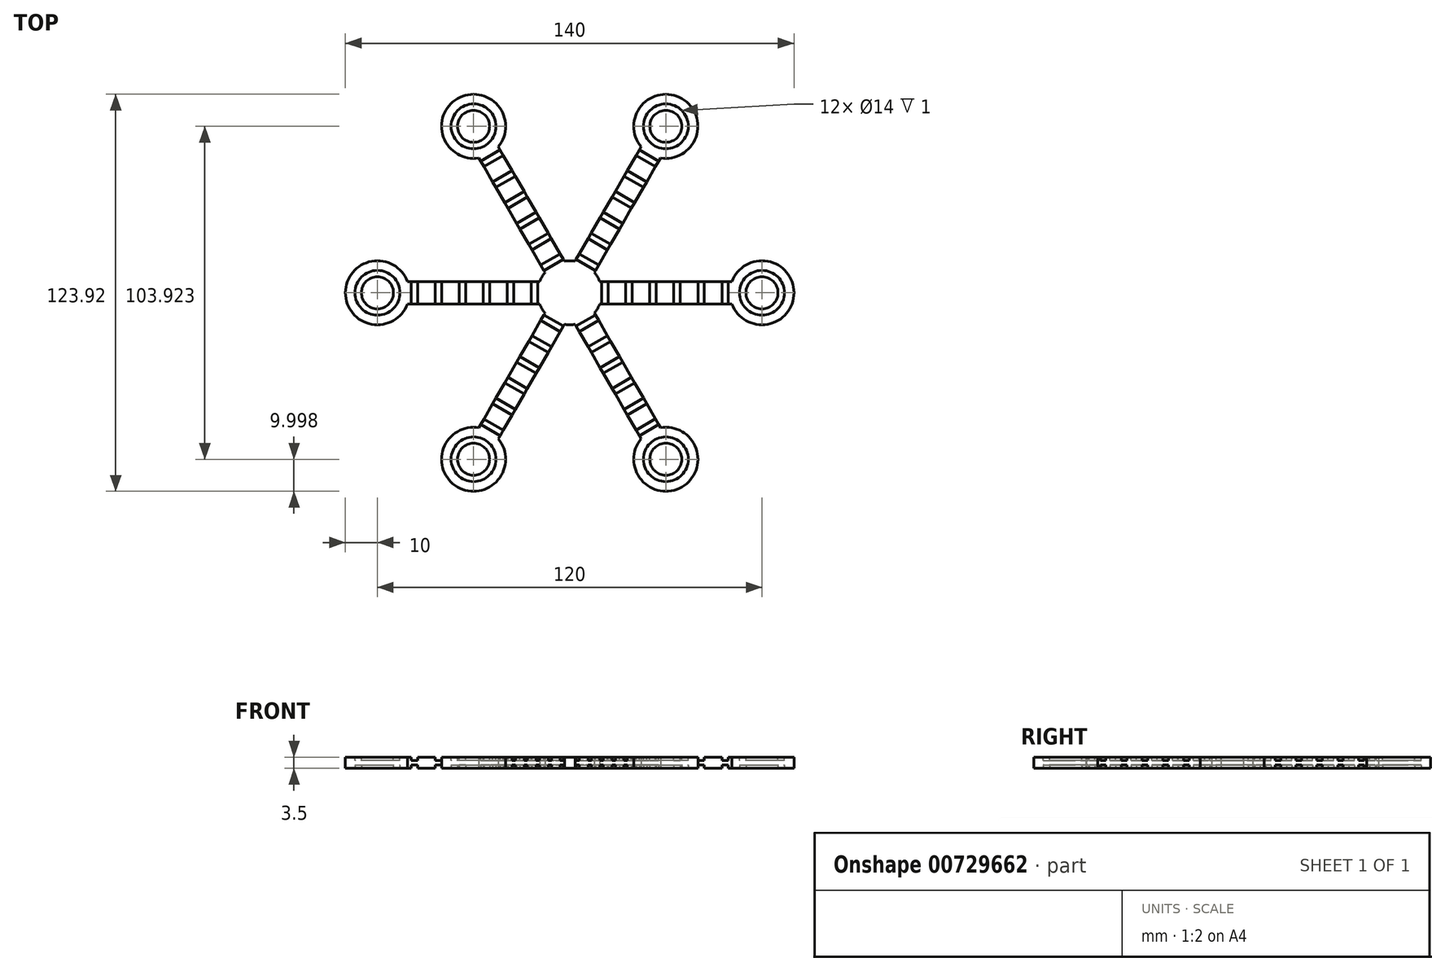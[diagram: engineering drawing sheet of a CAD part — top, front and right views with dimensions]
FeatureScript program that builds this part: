
annotation { "Feature Type Name" : "Feature", "Feature Type Description" : "" }
export const myFeature = defineFeature(function(context is Context, id is Id, definition is map)
    precondition{}
    {
        {
            var Q0;
            Q0=qCreatedBy(makeId("Top.planeOp"),FACE);
            var sketch = newSketch(context, id + "F0", { "sketchPlane" : qUnion([Q0])});
            skCircle(sketch, "E0", {"center": v(0, 0) * mm, "radius": 10 * mm});
            skLineSegment(sketch, "E1.bottom", {"start": v(9.37, 3.5) * mm, "end": v(60.15, 3.5) * mm});
            skLineSegment(sketch, "E1.top", {"start": v(9.37, -3.5) * mm, "end": v(59.85, -3.5) * mm});
            skLineSegment(sketch, "E1.right", {"start": v(60.15, 3.5) * mm, "end": v(59.85, -3.5) * mm});
            skCircle(sketch, "E2", {"center": v(60, 0) * mm, "radius": 10 * mm});
            skLineSegment(sketch, "E3.1.0", {"start": v(1.65, 9.86) * mm, "end": v(27.04, 53.84) * mm});
            skLineSegment(sketch, "E3.1.1", {"start": v(7.71, 6.37) * mm, "end": v(32.95, 50.08) * mm});
            skCircle(sketch, "E3.1.2", {"center": v(30, 51.96) * mm, "radius": 10 * mm});
            skLineSegment(sketch, "E3.1.3", {"start": v(27.04, 53.84) * mm, "end": v(32.95, 50.08) * mm});
            skLineSegment(sketch, "E3.2.0", {"start": v(-7.71, 6.36) * mm, "end": v(-33.1, 50.34) * mm});
            skLineSegment(sketch, "E3.2.1", {"start": v(-1.66, 9.86) * mm, "end": v(-26.9, 53.58) * mm});
            skCircle(sketch, "E3.2.2", {"center": v(-30, 51.96) * mm, "radius": 10 * mm});
            skLineSegment(sketch, "E3.2.3", {"start": v(-33.1, 50.34) * mm, "end": v(-26.9, 53.58) * mm});
            skLineSegment(sketch, "E3.3.0", {"start": v(-9.37, -3.5) * mm, "end": v(-60.15, -3.5) * mm});
            skLineSegment(sketch, "E3.3.1", {"start": v(-9.37, 3.5) * mm, "end": v(-59.85, 3.5) * mm});
            skCircle(sketch, "E3.3.2", {"center": v(-60, 0) * mm, "radius": 10 * mm});
            skLineSegment(sketch, "E3.3.3", {"start": v(-60.15, -3.5) * mm, "end": v(-59.85, 3.5) * mm});
            skLineSegment(sketch, "E3.4.0", {"start": v(-1.65, -9.86) * mm, "end": v(-27.04, -53.84) * mm});
            skLineSegment(sketch, "E3.4.1", {"start": v(-7.71, -6.37) * mm, "end": v(-32.95, -50.08) * mm});
            skCircle(sketch, "E3.4.2", {"center": v(-30, -51.96) * mm, "radius": 10 * mm});
            skLineSegment(sketch, "E3.4.3", {"start": v(-27.04, -53.84) * mm, "end": v(-32.95, -50.08) * mm});
            skLineSegment(sketch, "E3.5.0", {"start": v(7.71, -6.36) * mm, "end": v(33.1, -50.34) * mm});
            skLineSegment(sketch, "E3.5.1", {"start": v(1.66, -9.86) * mm, "end": v(26.9, -53.58) * mm});
            skCircle(sketch, "E3.5.2", {"center": v(30, -51.96) * mm, "radius": 10 * mm});
            skLineSegment(sketch, "E3.5.3", {"start": v(33.1, -50.34) * mm, "end": v(26.9, -53.58) * mm});
            skSolve(sketch);
        }
        {
            var Q0;
            {var subQ0=sQuery(id+"F0.wireOp",EDGE,"E3.3.3");Q0=makeQuery(id+"F0.imprint","IMPRINT",FACE,{"disambiguationData":[TD([[makeQuery(id+"F0.imprint","IMPRINT",EDGE,{"derivedFrom":subQ0}),1.0]])]});}
            var Q1;
            {var subQ0=sQuery(id+"F0.wireOp",EDGE,"E3.3.0");var subQ1=sQuery(id+"F0.wireOp",EDGE,"E0");var subQ2=makeQuery(id+"F0.imprint","INTERSECT",VERTEX,{"derivedFrom":[subQ1,subQ0]});Q1=makeQuery(id+"F0.imprint","IMPRINT",FACE,{"disambiguationData":[TD([[makeQuery(id+"F0.imprint","IMPRINT",EDGE,{"disambiguationData":[TD([[subQ2,1.0]])],"derivedFrom":subQ1}),-1.0]])]});}
            var Q2;
            {var subQ0=sQuery(id+"F0.wireOp",EDGE,"E3.2.3");Q2=makeQuery(id+"F0.imprint","IMPRINT",FACE,{"disambiguationData":[TD([[makeQuery(id+"F0.imprint","IMPRINT",EDGE,{"derivedFrom":subQ0}),1.0]])]});}
            var Q3;
            {var subQ0=sQuery(id+"F0.wireOp",EDGE,"E3.2.3");Q3=makeQuery(id+"F0.imprint","IMPRINT",FACE,{"disambiguationData":[TD([[makeQuery(id+"F0.imprint","IMPRINT",EDGE,{"derivedFrom":subQ0}),-1.0]])]});}
            var Q4;
            {var subQ0=sQuery(id+"F0.wireOp",EDGE,"E3.3.3");Q4=makeQuery(id+"F0.imprint","IMPRINT",FACE,{"disambiguationData":[TD([[makeQuery(id+"F0.imprint","IMPRINT",EDGE,{"derivedFrom":subQ0}),-1.0]])]});}
            var Q5;
            {var subQ0=sQuery(id+"F0.wireOp",EDGE,"E3.1.3");Q5=makeQuery(id+"F0.imprint","IMPRINT",FACE,{"disambiguationData":[TD([[makeQuery(id+"F0.imprint","IMPRINT",EDGE,{"derivedFrom":subQ0}),1.0]])]});}
            var Q6;
            {var subQ0=sQuery(id+"F0.wireOp",EDGE,"E3.1.3");Q6=makeQuery(id+"F0.imprint","IMPRINT",FACE,{"disambiguationData":[TD([[makeQuery(id+"F0.imprint","IMPRINT",EDGE,{"derivedFrom":subQ0}),-1.0]])]});}
            var Q7;
            {var subQ0=sQuery(id+"F0.wireOp",EDGE,"E3.1.0");var subQ1=sQuery(id+"F0.wireOp",EDGE,"E0");var subQ2=makeQuery(id+"F0.imprint","INTERSECT",VERTEX,{"derivedFrom":[subQ1,subQ0]});Q7=makeQuery(id+"F0.imprint","IMPRINT",FACE,{"disambiguationData":[TD([[makeQuery(id+"F0.imprint","IMPRINT",EDGE,{"disambiguationData":[TD([[subQ2,1.0]])],"derivedFrom":subQ1}),-1.0]])]});}
            var Q8;
            {var subQ0=sQuery(id+"F0.wireOp",EDGE,"E0");var subQ8=makeQuery(id+"F0.imprint","INTERSECT",VERTEX,{"derivedFrom":[subQ0,sQuery(id+"F0.wireOp",EDGE,"E1.bottom")]});Q8=makeQuery(id+"F0.imprint","IMPRINT",FACE,{"disambiguationData":[TD([[makeQuery(id+"F0.imprint","IMPRINT",EDGE,{"disambiguationData":[TD([[subQ8,-1.0]])],"derivedFrom":subQ0}),1.0]])]});}
            var Q9;
            {var subQ0=sQuery(id+"F0.wireOp",EDGE,"E1.bottom");var subQ1=sQuery(id+"F0.wireOp",EDGE,"E0");var subQ2=makeQuery(id+"F0.imprint","INTERSECT",VERTEX,{"derivedFrom":[subQ1,subQ0]});Q9=makeQuery(id+"F0.imprint","IMPRINT",FACE,{"disambiguationData":[TD([[makeQuery(id+"F0.imprint","IMPRINT",EDGE,{"disambiguationData":[TD([[subQ2,1.0]])],"derivedFrom":subQ1}),-1.0]])]});}
            var Q10;
            {var subQ0=sQuery(id+"F0.wireOp",EDGE,"E1.right");Q10=makeQuery(id+"F0.imprint","IMPRINT",FACE,{"disambiguationData":[TD([[makeQuery(id+"F0.imprint","IMPRINT",EDGE,{"derivedFrom":subQ0}),-1.0]])]});}
            var Q11;
            {var subQ0=sQuery(id+"F0.wireOp",EDGE,"E1.right");Q11=makeQuery(id+"F0.imprint","IMPRINT",FACE,{"disambiguationData":[TD([[makeQuery(id+"F0.imprint","IMPRINT",EDGE,{"derivedFrom":subQ0}),1.0]])]});}
            var Q12;
            {var subQ0=sQuery(id+"F0.wireOp",EDGE,"E3.5.3");Q12=makeQuery(id+"F0.imprint","IMPRINT",FACE,{"disambiguationData":[TD([[makeQuery(id+"F0.imprint","IMPRINT",EDGE,{"derivedFrom":subQ0}),1.0]])]});}
            var Q13;
            {var subQ0=sQuery(id+"F0.wireOp",EDGE,"E3.5.3");Q13=makeQuery(id+"F0.imprint","IMPRINT",FACE,{"disambiguationData":[TD([[makeQuery(id+"F0.imprint","IMPRINT",EDGE,{"derivedFrom":subQ0}),-1.0]])]});}
            var Q14;
            {var subQ0=sQuery(id+"F0.wireOp",EDGE,"E3.5.0");var subQ1=sQuery(id+"F0.wireOp",EDGE,"E0");var subQ2=makeQuery(id+"F0.imprint","INTERSECT",VERTEX,{"derivedFrom":[subQ1,subQ0]});Q14=makeQuery(id+"F0.imprint","IMPRINT",FACE,{"disambiguationData":[TD([[makeQuery(id+"F0.imprint","IMPRINT",EDGE,{"disambiguationData":[TD([[subQ2,1.0]])],"derivedFrom":subQ1}),-1.0]])]});}
            var Q15;
            {var subQ0=sQuery(id+"F0.wireOp",EDGE,"E3.4.0");var subQ1=sQuery(id+"F0.wireOp",EDGE,"E0");var subQ2=makeQuery(id+"F0.imprint","INTERSECT",VERTEX,{"derivedFrom":[subQ1,subQ0]});Q15=makeQuery(id+"F0.imprint","IMPRINT",FACE,{"disambiguationData":[TD([[makeQuery(id+"F0.imprint","IMPRINT",EDGE,{"disambiguationData":[TD([[subQ2,1.0]])],"derivedFrom":subQ1}),-1.0]])]});}
            var Q16;
            {var subQ0=sQuery(id+"F0.wireOp",EDGE,"E3.4.3");Q16=makeQuery(id+"F0.imprint","IMPRINT",FACE,{"disambiguationData":[TD([[makeQuery(id+"F0.imprint","IMPRINT",EDGE,{"derivedFrom":subQ0}),-1.0]])]});}
            var Q17;
            {var subQ0=sQuery(id+"F0.wireOp",EDGE,"E3.4.3");Q17=makeQuery(id+"F0.imprint","IMPRINT",FACE,{"disambiguationData":[TD([[makeQuery(id+"F0.imprint","IMPRINT",EDGE,{"derivedFrom":subQ0}),1.0]])]});}
            var Q18;
            {var subQ0=sQuery(id+"F0.wireOp",EDGE,"E3.2.0");var subQ1=sQuery(id+"F0.wireOp",EDGE,"E0");var subQ2=makeQuery(id+"F0.imprint","INTERSECT",VERTEX,{"derivedFrom":[subQ1,subQ0]});Q18=makeQuery(id+"F0.imprint","IMPRINT",FACE,{"disambiguationData":[TD([[makeQuery(id+"F0.imprint","IMPRINT",EDGE,{"disambiguationData":[TD([[subQ2,1.0]])],"derivedFrom":subQ1}),-1.0]])]});}
            extrude(context, id + "F1", {"entities" : qUnion([Q0, Q1, Q2, Q3, Q4, Q5, Q6, Q7, Q8, Q9, Q10, Q11, Q12, Q13, Q14, Q15, Q16, Q17, Q18]), "depth" : 3.5 * mm, "offsetDistance" : 25 * mm});
        }
        {
            var Q0;
            Q0=makeQuery(id+"F1.opExtrude","CAP_FACE",FACE,{"disambiguationData":[OSD([sQuery(id+"F0.wireOp",EDGE,"E0"),sQuery(id+"F0.wireOp",EDGE,"E1.bottom"),sQuery(id+"F0.wireOp",EDGE,"E1.top"),sQuery(id+"F0.wireOp",EDGE,"E2"),sQuery(id+"F0.wireOp",EDGE,"E3.1.0"),sQuery(id+"F0.wireOp",EDGE,"E3.1.1"),sQuery(id+"F0.wireOp",EDGE,"E3.1.2"),sQuery(id+"F0.wireOp",EDGE,"E3.2.0"),sQuery(id+"F0.wireOp",EDGE,"E3.2.1"),sQuery(id+"F0.wireOp",EDGE,"E3.2.2"),sQuery(id+"F0.wireOp",EDGE,"E3.3.0"),sQuery(id+"F0.wireOp",EDGE,"E3.3.1"),sQuery(id+"F0.wireOp",EDGE,"E3.3.2"),sQuery(id+"F0.wireOp",EDGE,"E3.4.0"),sQuery(id+"F0.wireOp",EDGE,"E3.4.1"),sQuery(id+"F0.wireOp",EDGE,"E3.4.2"),sQuery(id+"F0.wireOp",EDGE,"E3.5.0"),sQuery(id+"F0.wireOp",EDGE,"E3.5.1"),sQuery(id+"F0.wireOp",EDGE,"E3.5.2")])],"isStart":false});
            var sketch = newSketch(context, id + "F2", { "sketchPlane" : qUnion([Q0])});
            skLineSegment(sketch, "E4.bottom", {"start": v(10, 3.5) * mm, "end": v(12, 3.5) * mm});
            skLineSegment(sketch, "E4.top", {"start": v(10, -3.5) * mm, "end": v(12, -3.5) * mm});
            skLineSegment(sketch, "E4.left", {"start": v(10, 3.5) * mm, "end": v(10, -3.5) * mm});
            skLineSegment(sketch, "E4.right", {"start": v(12, 3.5) * mm, "end": v(12, -3.5) * mm});
            skLineSegment(sketch, "E5.1.0.0", {"start": v(17.5, -3.5) * mm, "end": v(19.5, -3.5) * mm});
            skLineSegment(sketch, "E5.1.0.1", {"start": v(17.5, 3.5) * mm, "end": v(19.5, 3.5) * mm});
            skLineSegment(sketch, "E5.1.0.2", {"start": v(17.5, 3.5) * mm, "end": v(17.5, -3.5) * mm});
            skLineSegment(sketch, "E5.1.0.3", {"start": v(19.5, 3.5) * mm, "end": v(19.5, -3.5) * mm});
            skLineSegment(sketch, "E5.2.0.0", {"start": v(25, -3.5) * mm, "end": v(27, -3.5) * mm});
            skLineSegment(sketch, "E5.2.0.1", {"start": v(25, 3.5) * mm, "end": v(27, 3.5) * mm});
            skLineSegment(sketch, "E5.2.0.2", {"start": v(25, 3.5) * mm, "end": v(25, -3.5) * mm});
            skLineSegment(sketch, "E5.2.0.3", {"start": v(27, 3.5) * mm, "end": v(27, -3.5) * mm});
            skLineSegment(sketch, "E5.3.0.0", {"start": v(32.5, -3.5) * mm, "end": v(34.5, -3.5) * mm});
            skLineSegment(sketch, "E5.3.0.1", {"start": v(32.5, 3.5) * mm, "end": v(34.5, 3.5) * mm});
            skLineSegment(sketch, "E5.3.0.2", {"start": v(32.5, 3.5) * mm, "end": v(32.5, -3.5) * mm});
            skLineSegment(sketch, "E5.3.0.3", {"start": v(34.5, 3.5) * mm, "end": v(34.5, -3.5) * mm});
            skLineSegment(sketch, "E5.4.0.0", {"start": v(40, -3.5) * mm, "end": v(42, -3.5) * mm});
            skLineSegment(sketch, "E5.4.0.1", {"start": v(40, 3.5) * mm, "end": v(42, 3.5) * mm});
            skLineSegment(sketch, "E5.4.0.2", {"start": v(40, 3.5) * mm, "end": v(40, -3.5) * mm});
            skLineSegment(sketch, "E5.4.0.3", {"start": v(42, 3.5) * mm, "end": v(42, -3.5) * mm});
            skLineSegment(sketch, "E5.direction1", {"start": v(10, -3.5) * mm, "end": v(17.5, -3.5) * mm, "construction": true});
            skLineSegment(sketch, "E6.1.0", {"start": v(5.72, 16.9) * mm, "end": v(11.78, 13.4) * mm});
            skLineSegment(sketch, "E6.1.1", {"start": v(1.97, 10.41) * mm, "end": v(2.97, 12.14) * mm});
            skLineSegment(sketch, "E6.1.2", {"start": v(6.72, 18.64) * mm, "end": v(12.78, 15.14) * mm});
            skLineSegment(sketch, "E6.1.3", {"start": v(15.53, 19.9) * mm, "end": v(16.53, 21.64) * mm});
            skLineSegment(sketch, "E6.1.4", {"start": v(1.97, 10.41) * mm, "end": v(8.03, 6.91) * mm});
            skLineSegment(sketch, "E6.1.5", {"start": v(9.47, 23.4) * mm, "end": v(10.47, 25.13) * mm});
            skLineSegment(sketch, "E6.1.6", {"start": v(8.03, 6.91) * mm, "end": v(11.78, 13.4) * mm, "construction": true});
            skLineSegment(sketch, "E6.1.7", {"start": v(2.97, 12.14) * mm, "end": v(9.03, 8.65) * mm});
            skLineSegment(sketch, "E6.1.8", {"start": v(14.22, 31.63) * mm, "end": v(20.28, 28.13) * mm});
            skLineSegment(sketch, "E6.1.9", {"start": v(9.47, 23.4) * mm, "end": v(15.53, 19.9) * mm});
            skLineSegment(sketch, "E6.1.10", {"start": v(17.97, 38.12) * mm, "end": v(24.03, 34.63) * mm});
            skLineSegment(sketch, "E6.1.11", {"start": v(11.78, 13.4) * mm, "end": v(12.78, 15.14) * mm});
            skLineSegment(sketch, "E6.1.12", {"start": v(13.22, 29.9) * mm, "end": v(14.22, 31.63) * mm});
            skLineSegment(sketch, "E6.1.13", {"start": v(10.47, 25.13) * mm, "end": v(16.53, 21.64) * mm});
            skLineSegment(sketch, "E6.1.14", {"start": v(16.97, 36.4) * mm, "end": v(23.03, 32.9) * mm});
            skLineSegment(sketch, "E6.1.15", {"start": v(5.72, 16.9) * mm, "end": v(6.72, 18.64) * mm});
            skLineSegment(sketch, "E6.1.16", {"start": v(13.22, 29.9) * mm, "end": v(19.28, 26.4) * mm});
            skLineSegment(sketch, "E6.1.17", {"start": v(19.28, 26.4) * mm, "end": v(20.28, 28.13) * mm});
            skLineSegment(sketch, "E6.1.18", {"start": v(16.97, 36.4) * mm, "end": v(17.97, 38.12) * mm});
            skLineSegment(sketch, "E6.1.19", {"start": v(23.03, 32.9) * mm, "end": v(24.03, 34.63) * mm});
            skLineSegment(sketch, "E6.1.20", {"start": v(8.03, 6.91) * mm, "end": v(9.03, 8.65) * mm});
            skLineSegment(sketch, "E6.2.0", {"start": v(-11.78, 13.4) * mm, "end": v(-5.72, 16.9) * mm});
            skLineSegment(sketch, "E6.2.1", {"start": v(-8.03, 6.91) * mm, "end": v(-9.03, 8.64) * mm});
            skLineSegment(sketch, "E6.2.2", {"start": v(-12.78, 15.14) * mm, "end": v(-6.72, 18.63) * mm});
            skLineSegment(sketch, "E6.2.3", {"start": v(-9.47, 23.4) * mm, "end": v(-10.47, 25.13) * mm});
            skLineSegment(sketch, "E6.2.4", {"start": v(-8.03, 6.91) * mm, "end": v(-1.97, 10.4) * mm});
            skLineSegment(sketch, "E6.2.5", {"start": v(-15.53, 19.9) * mm, "end": v(-16.53, 21.63) * mm});
            skLineSegment(sketch, "E6.2.6", {"start": v(-1.97, 10.4) * mm, "end": v(-5.72, 16.9) * mm, "construction": true});
            skLineSegment(sketch, "E6.2.7", {"start": v(-9.03, 8.64) * mm, "end": v(-2.97, 12.14) * mm});
            skLineSegment(sketch, "E6.2.8", {"start": v(-20.28, 28.13) * mm, "end": v(-14.22, 31.62) * mm});
            skLineSegment(sketch, "E6.2.9", {"start": v(-15.53, 19.9) * mm, "end": v(-9.47, 23.4) * mm});
            skLineSegment(sketch, "E6.2.10", {"start": v(-24.03, 34.62) * mm, "end": v(-17.97, 38.12) * mm});
            skLineSegment(sketch, "E6.2.11", {"start": v(-5.72, 16.9) * mm, "end": v(-6.72, 18.63) * mm});
            skLineSegment(sketch, "E6.2.12", {"start": v(-19.28, 26.4) * mm, "end": v(-20.28, 28.13) * mm});
            skLineSegment(sketch, "E6.2.13", {"start": v(-16.53, 21.63) * mm, "end": v(-10.47, 25.13) * mm});
            skLineSegment(sketch, "E6.2.14", {"start": v(-23.03, 32.9) * mm, "end": v(-16.97, 36.39) * mm});
            skLineSegment(sketch, "E6.2.15", {"start": v(-11.78, 13.4) * mm, "end": v(-12.78, 15.14) * mm});
            skLineSegment(sketch, "E6.2.16", {"start": v(-19.28, 26.4) * mm, "end": v(-13.22, 29.9) * mm});
            skLineSegment(sketch, "E6.2.17", {"start": v(-13.22, 29.9) * mm, "end": v(-14.22, 31.62) * mm});
            skLineSegment(sketch, "E6.2.18", {"start": v(-23.03, 32.9) * mm, "end": v(-24.03, 34.62) * mm});
            skLineSegment(sketch, "E6.2.19", {"start": v(-16.97, 36.39) * mm, "end": v(-17.97, 38.12) * mm});
            skLineSegment(sketch, "E6.2.20", {"start": v(-1.97, 10.4) * mm, "end": v(-2.97, 12.14) * mm});
            skLineSegment(sketch, "E6.3.0", {"start": v(-17.5, -3.5) * mm, "end": v(-17.5, 3.5) * mm});
            skLineSegment(sketch, "E6.3.1", {"start": v(-10, -3.5) * mm, "end": v(-12, -3.5) * mm});
            skLineSegment(sketch, "E6.3.2", {"start": v(-19.5, -3.5) * mm, "end": v(-19.5, 3.5) * mm});
            skLineSegment(sketch, "E6.3.3", {"start": v(-25, 3.5) * mm, "end": v(-27, 3.5) * mm});
            skLineSegment(sketch, "E6.3.4", {"start": v(-10, -3.5) * mm, "end": v(-10, 3.5) * mm});
            skLineSegment(sketch, "E6.3.5", {"start": v(-25, -3.5) * mm, "end": v(-27, -3.5) * mm});
            skLineSegment(sketch, "E6.3.6", {"start": v(-10, 3.5) * mm, "end": v(-17.5, 3.5) * mm, "construction": true});
            skLineSegment(sketch, "E6.3.7", {"start": v(-12, -3.5) * mm, "end": v(-12, 3.5) * mm});
            skLineSegment(sketch, "E6.3.8", {"start": v(-34.5, -3.5) * mm, "end": v(-34.5, 3.5) * mm});
            skLineSegment(sketch, "E6.3.9", {"start": v(-25, -3.5) * mm, "end": v(-25, 3.5) * mm});
            skLineSegment(sketch, "E6.3.10", {"start": v(-42, -3.5) * mm, "end": v(-42, 3.5) * mm});
            skLineSegment(sketch, "E6.3.11", {"start": v(-17.5, 3.5) * mm, "end": v(-19.5, 3.5) * mm});
            skLineSegment(sketch, "E6.3.12", {"start": v(-32.5, -3.5) * mm, "end": v(-34.5, -3.5) * mm});
            skLineSegment(sketch, "E6.3.13", {"start": v(-27, -3.5) * mm, "end": v(-27, 3.5) * mm});
            skLineSegment(sketch, "E6.3.14", {"start": v(-40, -3.5) * mm, "end": v(-40, 3.5) * mm});
            skLineSegment(sketch, "E6.3.15", {"start": v(-17.5, -3.5) * mm, "end": v(-19.5, -3.5) * mm});
            skLineSegment(sketch, "E6.3.16", {"start": v(-32.5, -3.5) * mm, "end": v(-32.5, 3.5) * mm});
            skLineSegment(sketch, "E6.3.17", {"start": v(-32.5, 3.5) * mm, "end": v(-34.5, 3.5) * mm});
            skLineSegment(sketch, "E6.3.18", {"start": v(-40, -3.5) * mm, "end": v(-42, -3.5) * mm});
            skLineSegment(sketch, "E6.3.19", {"start": v(-40, 3.5) * mm, "end": v(-42, 3.5) * mm});
            skLineSegment(sketch, "E6.3.20", {"start": v(-10, 3.5) * mm, "end": v(-12, 3.5) * mm});
            skLineSegment(sketch, "E6.4.0", {"start": v(-5.72, -16.9) * mm, "end": v(-11.78, -13.4) * mm});
            skLineSegment(sketch, "E6.4.1", {"start": v(-1.97, -10.41) * mm, "end": v(-2.97, -12.14) * mm});
            skLineSegment(sketch, "E6.4.2", {"start": v(-6.72, -18.64) * mm, "end": v(-12.78, -15.14) * mm});
            skLineSegment(sketch, "E6.4.3", {"start": v(-15.53, -19.9) * mm, "end": v(-16.53, -21.64) * mm});
            skLineSegment(sketch, "E6.4.4", {"start": v(-1.97, -10.41) * mm, "end": v(-8.03, -6.91) * mm});
            skLineSegment(sketch, "E6.4.5", {"start": v(-9.47, -23.4) * mm, "end": v(-10.47, -25.13) * mm});
            skLineSegment(sketch, "E6.4.6", {"start": v(-8.03, -6.91) * mm, "end": v(-11.78, -13.4) * mm, "construction": true});
            skLineSegment(sketch, "E6.4.7", {"start": v(-2.97, -12.14) * mm, "end": v(-9.03, -8.65) * mm});
            skLineSegment(sketch, "E6.4.8", {"start": v(-14.22, -31.63) * mm, "end": v(-20.28, -28.13) * mm});
            skLineSegment(sketch, "E6.4.9", {"start": v(-9.47, -23.4) * mm, "end": v(-15.53, -19.9) * mm});
            skLineSegment(sketch, "E6.4.10", {"start": v(-17.97, -38.12) * mm, "end": v(-24.03, -34.63) * mm});
            skLineSegment(sketch, "E6.4.11", {"start": v(-11.78, -13.4) * mm, "end": v(-12.78, -15.14) * mm});
            skLineSegment(sketch, "E6.4.12", {"start": v(-13.22, -29.9) * mm, "end": v(-14.22, -31.63) * mm});
            skLineSegment(sketch, "E6.4.13", {"start": v(-10.47, -25.13) * mm, "end": v(-16.53, -21.64) * mm});
            skLineSegment(sketch, "E6.4.14", {"start": v(-16.97, -36.4) * mm, "end": v(-23.03, -32.9) * mm});
            skLineSegment(sketch, "E6.4.15", {"start": v(-5.72, -16.9) * mm, "end": v(-6.72, -18.64) * mm});
            skLineSegment(sketch, "E6.4.16", {"start": v(-13.22, -29.9) * mm, "end": v(-19.28, -26.4) * mm});
            skLineSegment(sketch, "E6.4.17", {"start": v(-19.28, -26.4) * mm, "end": v(-20.28, -28.13) * mm});
            skLineSegment(sketch, "E6.4.18", {"start": v(-16.97, -36.4) * mm, "end": v(-17.97, -38.12) * mm});
            skLineSegment(sketch, "E6.4.19", {"start": v(-23.03, -32.9) * mm, "end": v(-24.03, -34.63) * mm});
            skLineSegment(sketch, "E6.4.20", {"start": v(-8.03, -6.91) * mm, "end": v(-9.03, -8.65) * mm});
            skLineSegment(sketch, "E6.5.0", {"start": v(11.78, -13.4) * mm, "end": v(5.72, -16.9) * mm});
            skLineSegment(sketch, "E6.5.1", {"start": v(8.03, -6.91) * mm, "end": v(9.03, -8.64) * mm});
            skLineSegment(sketch, "E6.5.2", {"start": v(12.78, -15.14) * mm, "end": v(6.72, -18.63) * mm});
            skLineSegment(sketch, "E6.5.3", {"start": v(9.47, -23.4) * mm, "end": v(10.47, -25.13) * mm});
            skLineSegment(sketch, "E6.5.4", {"start": v(8.03, -6.91) * mm, "end": v(1.97, -10.4) * mm});
            skLineSegment(sketch, "E6.5.5", {"start": v(15.53, -19.9) * mm, "end": v(16.53, -21.63) * mm});
            skLineSegment(sketch, "E6.5.6", {"start": v(1.97, -10.4) * mm, "end": v(5.72, -16.9) * mm, "construction": true});
            skLineSegment(sketch, "E6.5.7", {"start": v(9.03, -8.64) * mm, "end": v(2.97, -12.14) * mm});
            skLineSegment(sketch, "E6.5.8", {"start": v(20.28, -28.13) * mm, "end": v(14.22, -31.62) * mm});
            skLineSegment(sketch, "E6.5.9", {"start": v(15.53, -19.9) * mm, "end": v(9.47, -23.4) * mm});
            skLineSegment(sketch, "E6.5.10", {"start": v(24.03, -34.62) * mm, "end": v(17.97, -38.12) * mm});
            skLineSegment(sketch, "E6.5.11", {"start": v(5.72, -16.9) * mm, "end": v(6.72, -18.63) * mm});
            skLineSegment(sketch, "E6.5.12", {"start": v(19.28, -26.4) * mm, "end": v(20.28, -28.13) * mm});
            skLineSegment(sketch, "E6.5.13", {"start": v(16.53, -21.63) * mm, "end": v(10.47, -25.13) * mm});
            skLineSegment(sketch, "E6.5.14", {"start": v(23.03, -32.9) * mm, "end": v(16.97, -36.39) * mm});
            skLineSegment(sketch, "E6.5.15", {"start": v(11.78, -13.4) * mm, "end": v(12.78, -15.14) * mm});
            skLineSegment(sketch, "E6.5.16", {"start": v(19.28, -26.4) * mm, "end": v(13.22, -29.9) * mm});
            skLineSegment(sketch, "E6.5.17", {"start": v(13.22, -29.9) * mm, "end": v(14.22, -31.62) * mm});
            skLineSegment(sketch, "E6.5.18", {"start": v(23.03, -32.9) * mm, "end": v(24.03, -34.62) * mm});
            skLineSegment(sketch, "E6.5.19", {"start": v(16.97, -36.39) * mm, "end": v(17.97, -38.12) * mm});
            skLineSegment(sketch, "E6.5.20", {"start": v(1.97, -10.4) * mm, "end": v(2.97, -12.14) * mm});
            skPoint(sketch, "E6.center", {"position": v(0, 0) * mm});
            skCircle(sketch, "E7", {"center": v(60, 0) * mm, "radius": 7 * mm});
            skCircle(sketch, "E8", {"center": v(60, 0) * mm, "radius": 5 * mm});
            skCircle(sketch, "E9.1.0", {"center": v(30, 51.96) * mm, "radius": 7 * mm});
            skCircle(sketch, "E9.1.1", {"center": v(30, 51.96) * mm, "radius": 5 * mm});
            skCircle(sketch, "E9.2.0", {"center": v(-30, 51.96) * mm, "radius": 7 * mm});
            skCircle(sketch, "E9.2.1", {"center": v(-30, 51.96) * mm, "radius": 5 * mm});
            skCircle(sketch, "E9.3.0", {"center": v(-60, 0) * mm, "radius": 7 * mm});
            skCircle(sketch, "E9.3.1", {"center": v(-60, 0) * mm, "radius": 5 * mm});
            skCircle(sketch, "E9.4.0", {"center": v(-30, -51.96) * mm, "radius": 7 * mm});
            skCircle(sketch, "E9.4.1", {"center": v(-30, -51.96) * mm, "radius": 5 * mm});
            skCircle(sketch, "E9.5.0", {"center": v(30, -51.96) * mm, "radius": 7 * mm});
            skCircle(sketch, "E9.5.1", {"center": v(30, -51.96) * mm, "radius": 5 * mm});
            skLineSegment(sketch, "E10.0.5.0", {"start": v(47.5, -3.5) * mm, "end": v(49.5, -3.5) * mm});
            skLineSegment(sketch, "E10.3.5.0", {"start": v(47.5, 3.5) * mm, "end": v(49.5, 3.5) * mm});
            skLineSegment(sketch, "E10.6.5.0", {"start": v(47.5, 3.5) * mm, "end": v(47.5, -3.5) * mm});
            skLineSegment(sketch, "E10.9.5.0", {"start": v(49.5, 3.5) * mm, "end": v(49.5, -3.5) * mm});
            skLineSegment(sketch, "E11.1.0", {"start": v(26.78, 39.39) * mm, "end": v(27.78, 41.12) * mm});
            skLineSegment(sketch, "E11.1.1", {"start": v(20.72, 42.89) * mm, "end": v(26.78, 39.39) * mm});
            skLineSegment(sketch, "E11.1.2", {"start": v(21.72, 44.62) * mm, "end": v(27.78, 41.12) * mm});
            skLineSegment(sketch, "E11.1.3", {"start": v(20.72, 42.89) * mm, "end": v(21.72, 44.62) * mm});
            skLineSegment(sketch, "E11.2.0", {"start": v(-20.72, 42.88) * mm, "end": v(-21.72, 44.61) * mm});
            skLineSegment(sketch, "E11.2.1", {"start": v(-26.78, 39.39) * mm, "end": v(-20.72, 42.88) * mm});
            skLineSegment(sketch, "E11.2.2", {"start": v(-27.78, 41.12) * mm, "end": v(-21.72, 44.61) * mm});
            skLineSegment(sketch, "E11.2.3", {"start": v(-26.78, 39.39) * mm, "end": v(-27.78, 41.12) * mm});
            skLineSegment(sketch, "E11.3.0", {"start": v(-47.5, 3.5) * mm, "end": v(-49.5, 3.5) * mm});
            skLineSegment(sketch, "E11.3.1", {"start": v(-47.5, -3.5) * mm, "end": v(-47.5, 3.5) * mm});
            skLineSegment(sketch, "E11.3.2", {"start": v(-49.5, -3.5) * mm, "end": v(-49.5, 3.5) * mm});
            skLineSegment(sketch, "E11.3.3", {"start": v(-47.5, -3.5) * mm, "end": v(-49.5, -3.5) * mm});
            skLineSegment(sketch, "E11.4.0", {"start": v(-26.78, -39.39) * mm, "end": v(-27.78, -41.12) * mm});
            skLineSegment(sketch, "E11.4.1", {"start": v(-20.72, -42.89) * mm, "end": v(-26.78, -39.39) * mm});
            skLineSegment(sketch, "E11.4.2", {"start": v(-21.72, -44.62) * mm, "end": v(-27.78, -41.12) * mm});
            skLineSegment(sketch, "E11.4.3", {"start": v(-20.72, -42.89) * mm, "end": v(-21.72, -44.62) * mm});
            skLineSegment(sketch, "E11.5.0", {"start": v(20.72, -42.88) * mm, "end": v(21.72, -44.61) * mm});
            skLineSegment(sketch, "E11.5.1", {"start": v(26.78, -39.39) * mm, "end": v(20.72, -42.88) * mm});
            skLineSegment(sketch, "E11.5.2", {"start": v(27.78, -41.12) * mm, "end": v(21.72, -44.61) * mm});
            skLineSegment(sketch, "E11.5.3", {"start": v(26.78, -39.39) * mm, "end": v(27.78, -41.12) * mm});
            skSolve(sketch);
        }
        {
            var Q0;
            Q0=makeQuery(id+"F2.imprint","IMPRINT",FACE,{"disambiguationData":[TD([[makeQuery(id+"F2.imprint","IMPRINT",EDGE,{"derivedFrom":sQuery(id+"F2.wireOp",EDGE,"E6.4.10")}),-1.0]])]});
            var Q1;
            Q1=makeQuery(id+"F2.imprint","IMPRINT",FACE,{"disambiguationData":[TD([[makeQuery(id+"F2.imprint","IMPRINT",EDGE,{"derivedFrom":sQuery(id+"F2.wireOp",EDGE,"E6.4.8")}),-1.0]])]});
            var Q2;
            Q2=makeQuery(id+"F2.imprint","IMPRINT",FACE,{"disambiguationData":[TD([[makeQuery(id+"F2.imprint","IMPRINT",EDGE,{"derivedFrom":sQuery(id+"F2.wireOp",EDGE,"E6.4.3")}),1.0]])]});
            var Q3;
            Q3=makeQuery(id+"F2.imprint","IMPRINT",FACE,{"disambiguationData":[TD([[makeQuery(id+"F2.imprint","IMPRINT",EDGE,{"derivedFrom":sQuery(id+"F2.wireOp",EDGE,"E6.4.0")}),1.0]])]});
            var Q4;
            Q4=makeQuery(id+"F2.imprint","IMPRINT",FACE,{"disambiguationData":[TD([[makeQuery(id+"F2.imprint","IMPRINT",EDGE,{"derivedFrom":sQuery(id+"F2.wireOp",EDGE,"E6.4.1")}),-1.0]])]});
            var Q5;
            Q5=makeQuery(id+"F2.imprint","IMPRINT",FACE,{"disambiguationData":[TD([[makeQuery(id+"F2.imprint","IMPRINT",EDGE,{"derivedFrom":sQuery(id+"F2.wireOp",EDGE,"E6.5.1")}),-1.0]])]});
            var Q6;
            Q6=makeQuery(id+"F2.imprint","IMPRINT",FACE,{"disambiguationData":[TD([[makeQuery(id+"F2.imprint","IMPRINT",EDGE,{"derivedFrom":sQuery(id+"F2.wireOp",EDGE,"E6.5.0")}),1.0]])]});
            var Q7;
            Q7=makeQuery(id+"F2.imprint","IMPRINT",FACE,{"disambiguationData":[TD([[makeQuery(id+"F2.imprint","IMPRINT",EDGE,{"derivedFrom":sQuery(id+"F2.wireOp",EDGE,"E6.5.3")}),1.0]])]});
            var Q8;
            Q8=makeQuery(id+"F2.imprint","IMPRINT",FACE,{"disambiguationData":[TD([[makeQuery(id+"F2.imprint","IMPRINT",EDGE,{"derivedFrom":sQuery(id+"F2.wireOp",EDGE,"E6.5.8")}),-1.0]])]});
            var Q9;
            Q9=makeQuery(id+"F2.imprint","IMPRINT",FACE,{"disambiguationData":[TD([[makeQuery(id+"F2.imprint","IMPRINT",EDGE,{"derivedFrom":sQuery(id+"F2.wireOp",EDGE,"E6.5.10")}),-1.0]])]});
            var Q10;
            Q10=makeQuery(id+"F2.imprint","IMPRINT",FACE,{"disambiguationData":[TD([[makeQuery(id+"F2.imprint","IMPRINT",EDGE,{"derivedFrom":sQuery(id+"F2.wireOp",EDGE,"E5.4.0.0")}),1.0]])]});
            var Q11;
            Q11=makeQuery(id+"F2.imprint","IMPRINT",FACE,{"disambiguationData":[TD([[makeQuery(id+"F2.imprint","IMPRINT",EDGE,{"derivedFrom":sQuery(id+"F2.wireOp",EDGE,"E5.2.0.0")}),1.0]])]});
            var Q12;
            Q12=makeQuery(id+"F2.imprint","IMPRINT",FACE,{"disambiguationData":[TD([[makeQuery(id+"F2.imprint","IMPRINT",EDGE,{"derivedFrom":sQuery(id+"F2.wireOp",EDGE,"E5.1.0.0")}),1.0]])]});
            var Q13;
            Q13=makeQuery(id+"F2.imprint","IMPRINT",FACE,{"disambiguationData":[TD([[makeQuery(id+"F2.imprint","IMPRINT",EDGE,{"derivedFrom":sQuery(id+"F2.wireOp",EDGE,"E4.bottom")}),-1.0]])]});
            var Q14;
            Q14=makeQuery(id+"F2.imprint","IMPRINT",FACE,{"disambiguationData":[TD([[makeQuery(id+"F2.imprint","IMPRINT",EDGE,{"derivedFrom":sQuery(id+"F2.wireOp",EDGE,"E6.1.10")}),-1.0]])]});
            var Q15;
            Q15=makeQuery(id+"F2.imprint","IMPRINT",FACE,{"disambiguationData":[TD([[makeQuery(id+"F2.imprint","IMPRINT",EDGE,{"derivedFrom":sQuery(id+"F2.wireOp",EDGE,"E6.1.8")}),-1.0]])]});
            var Q16;
            Q16=makeQuery(id+"F2.imprint","IMPRINT",FACE,{"disambiguationData":[TD([[makeQuery(id+"F2.imprint","IMPRINT",EDGE,{"derivedFrom":sQuery(id+"F2.wireOp",EDGE,"E6.1.3")}),1.0]])]});
            var Q17;
            Q17=makeQuery(id+"F2.imprint","IMPRINT",FACE,{"disambiguationData":[TD([[makeQuery(id+"F2.imprint","IMPRINT",EDGE,{"derivedFrom":sQuery(id+"F2.wireOp",EDGE,"E6.1.0")}),1.0]])]});
            var Q18;
            Q18=makeQuery(id+"F2.imprint","IMPRINT",FACE,{"disambiguationData":[TD([[makeQuery(id+"F2.imprint","IMPRINT",EDGE,{"derivedFrom":sQuery(id+"F2.wireOp",EDGE,"E6.1.1")}),-1.0]])]});
            var Q19;
            Q19=makeQuery(id+"F2.imprint","IMPRINT",FACE,{"disambiguationData":[TD([[makeQuery(id+"F2.imprint","IMPRINT",EDGE,{"derivedFrom":sQuery(id+"F2.wireOp",EDGE,"E6.2.1")}),-1.0]])]});
            var Q20;
            Q20=makeQuery(id+"F2.imprint","IMPRINT",FACE,{"disambiguationData":[TD([[makeQuery(id+"F2.imprint","IMPRINT",EDGE,{"derivedFrom":sQuery(id+"F2.wireOp",EDGE,"E6.2.0")}),1.0]])]});
            var Q21;
            Q21=makeQuery(id+"F2.imprint","IMPRINT",FACE,{"disambiguationData":[TD([[makeQuery(id+"F2.imprint","IMPRINT",EDGE,{"derivedFrom":sQuery(id+"F2.wireOp",EDGE,"E6.2.3")}),1.0]])]});
            var Q22;
            Q22=makeQuery(id+"F2.imprint","IMPRINT",FACE,{"disambiguationData":[TD([[makeQuery(id+"F2.imprint","IMPRINT",EDGE,{"derivedFrom":sQuery(id+"F2.wireOp",EDGE,"E6.2.8")}),-1.0]])]});
            var Q23;
            Q23=makeQuery(id+"F2.imprint","IMPRINT",FACE,{"disambiguationData":[TD([[makeQuery(id+"F2.imprint","IMPRINT",EDGE,{"derivedFrom":sQuery(id+"F2.wireOp",EDGE,"E6.2.10")}),-1.0]])]});
            var Q24;
            Q24=makeQuery(id+"F2.imprint","IMPRINT",FACE,{"disambiguationData":[TD([[makeQuery(id+"F2.imprint","IMPRINT",EDGE,{"derivedFrom":sQuery(id+"F2.wireOp",EDGE,"E6.3.1")}),-1.0]])]});
            var Q25;
            Q25=makeQuery(id+"F2.imprint","IMPRINT",FACE,{"disambiguationData":[TD([[makeQuery(id+"F2.imprint","IMPRINT",EDGE,{"derivedFrom":sQuery(id+"F2.wireOp",EDGE,"E6.3.0")}),1.0]])]});
            var Q26;
            Q26=makeQuery(id+"F2.imprint","IMPRINT",FACE,{"disambiguationData":[TD([[makeQuery(id+"F2.imprint","IMPRINT",EDGE,{"derivedFrom":sQuery(id+"F2.wireOp",EDGE,"E6.3.3")}),1.0]])]});
            var Q27;
            Q27=makeQuery(id+"F2.imprint","IMPRINT",FACE,{"disambiguationData":[TD([[makeQuery(id+"F2.imprint","IMPRINT",EDGE,{"derivedFrom":sQuery(id+"F2.wireOp",EDGE,"E6.3.8")}),-1.0]])]});
            var Q28;
            Q28=makeQuery(id+"F2.imprint","IMPRINT",FACE,{"disambiguationData":[TD([[makeQuery(id+"F2.imprint","IMPRINT",EDGE,{"derivedFrom":sQuery(id+"F2.wireOp",EDGE,"E6.3.10")}),-1.0]])]});
            var Q29;
            Q29=makeQuery(id+"F2.imprint","IMPRINT",FACE,{"disambiguationData":[TD([[makeQuery(id+"F2.imprint","IMPRINT",EDGE,{"derivedFrom":sQuery(id+"F2.wireOp",EDGE,"E9.2.0")}),1.0]])]});
            var Q30;
            Q30=makeQuery(id+"F2.imprint","IMPRINT",FACE,{"disambiguationData":[TD([[makeQuery(id+"F2.imprint","IMPRINT",EDGE,{"derivedFrom":sQuery(id+"F2.wireOp",EDGE,"E9.1.0")}),1.0]])]});
            var Q31;
            Q31=makeQuery(id+"F2.imprint","IMPRINT",FACE,{"disambiguationData":[TD([[makeQuery(id+"F2.imprint","IMPRINT",EDGE,{"derivedFrom":sQuery(id+"F2.wireOp",EDGE,"E7")}),1.0]])]});
            var Q32;
            Q32=makeQuery(id+"F2.imprint","IMPRINT",FACE,{"disambiguationData":[TD([[makeQuery(id+"F2.imprint","IMPRINT",EDGE,{"derivedFrom":sQuery(id+"F2.wireOp",EDGE,"E9.5.0")}),1.0]])]});
            var Q33;
            Q33=makeQuery(id+"F2.imprint","IMPRINT",FACE,{"disambiguationData":[TD([[makeQuery(id+"F2.imprint","IMPRINT",EDGE,{"derivedFrom":sQuery(id+"F2.wireOp",EDGE,"E9.4.0")}),1.0]])]});
            var Q34;
            Q34=makeQuery(id+"F2.imprint","IMPRINT",FACE,{"disambiguationData":[TD([[makeQuery(id+"F2.imprint","IMPRINT",EDGE,{"derivedFrom":sQuery(id+"F2.wireOp",EDGE,"E9.3.0")}),1.0]])]});
            var Q35;
            Q35=makeQuery(id+"F2.imprint","IMPRINT",FACE,{"disambiguationData":[TD([[makeQuery(id+"F2.imprint","IMPRINT",EDGE,{"derivedFrom":sQuery(id+"F2.wireOp",EDGE,"E5.3.0.0")}),1.0]])]});
            var Q36;
            Q36=makeQuery(id+"F2.imprint","IMPRINT",FACE,{"disambiguationData":[TD([[makeQuery(id+"F2.imprint","IMPRINT",EDGE,{"derivedFrom":sQuery(id+"F2.wireOp",EDGE,"E10.0.5.0")}),1.0]])]});
            var Q37;
            Q37=makeQuery(id+"F2.imprint","IMPRINT",FACE,{"disambiguationData":[TD([[makeQuery(id+"F2.imprint","IMPRINT",EDGE,{"derivedFrom":sQuery(id+"F2.wireOp",EDGE,"E11.1.0")}),1.0]])]});
            var Q38;
            Q38=makeQuery(id+"F2.imprint","IMPRINT",FACE,{"disambiguationData":[TD([[makeQuery(id+"F2.imprint","IMPRINT",EDGE,{"derivedFrom":sQuery(id+"F2.wireOp",EDGE,"E11.2.0")}),1.0]])]});
            var Q39;
            Q39=makeQuery(id+"F2.imprint","IMPRINT",FACE,{"disambiguationData":[TD([[makeQuery(id+"F2.imprint","IMPRINT",EDGE,{"derivedFrom":sQuery(id+"F2.wireOp",EDGE,"E11.3.0")}),1.0]])]});
            var Q40;
            Q40=makeQuery(id+"F2.imprint","IMPRINT",FACE,{"disambiguationData":[TD([[makeQuery(id+"F2.imprint","IMPRINT",EDGE,{"derivedFrom":sQuery(id+"F2.wireOp",EDGE,"E11.4.0")}),1.0]])]});
            var Q41;
            Q41=makeQuery(id+"F2.imprint","IMPRINT",FACE,{"disambiguationData":[TD([[makeQuery(id+"F2.imprint","IMPRINT",EDGE,{"derivedFrom":sQuery(id+"F2.wireOp",EDGE,"E11.5.0")}),1.0]])]});
            extrude(context, id + "F3", {"entities" : qUnion([Q0, Q1, Q2, Q3, Q4, Q5, Q6, Q7, Q8, Q9, Q10, Q11, Q12, Q13, Q14, Q15, Q16, Q17, Q18, Q19, Q20, Q21, Q22, Q23, Q24, Q25, Q26, Q27, Q28, Q29, Q30, Q31, Q32, Q33, Q34, Q35, Q36, Q37, Q38, Q39, Q40, Q41]), "operationType" : NewBodyOperationType.REMOVE, "oppositeDirection" : true, "depth" : 1 * mm, "offsetDistance" : 25 * mm});
        }
        {
            var Q0;
            Q0=makeQuery(id+"F1.opExtrude","CAP_FACE",FACE,{"disambiguationData":[OSD([sQuery(id+"F0.wireOp",EDGE,"E0"),sQuery(id+"F0.wireOp",EDGE,"E1.bottom"),sQuery(id+"F0.wireOp",EDGE,"E1.top"),sQuery(id+"F0.wireOp",EDGE,"E2"),sQuery(id+"F0.wireOp",EDGE,"E3.1.0"),sQuery(id+"F0.wireOp",EDGE,"E3.1.1"),sQuery(id+"F0.wireOp",EDGE,"E3.1.2"),sQuery(id+"F0.wireOp",EDGE,"E3.2.0"),sQuery(id+"F0.wireOp",EDGE,"E3.2.1"),sQuery(id+"F0.wireOp",EDGE,"E3.2.2"),sQuery(id+"F0.wireOp",EDGE,"E3.3.0"),sQuery(id+"F0.wireOp",EDGE,"E3.3.1"),sQuery(id+"F0.wireOp",EDGE,"E3.3.2"),sQuery(id+"F0.wireOp",EDGE,"E3.4.0"),sQuery(id+"F0.wireOp",EDGE,"E3.4.1"),sQuery(id+"F0.wireOp",EDGE,"E3.4.2"),sQuery(id+"F0.wireOp",EDGE,"E3.5.0"),sQuery(id+"F0.wireOp",EDGE,"E3.5.1"),sQuery(id+"F0.wireOp",EDGE,"E3.5.2")])],"isStart":true});
            var sketch = newSketch(context, id + "F4", { "sketchPlane" : qUnion([Q0])});
            skCircle(sketch, "E12", {"center": v(60, 0) * mm, "radius": 5 * mm});
            skCircle(sketch, "E13", {"center": v(60, 0) * mm, "radius": 7 * mm});
            skCircle(sketch, "E14.1.0", {"center": v(30, 51.96) * mm, "radius": 5 * mm});
            skCircle(sketch, "E14.1.1", {"center": v(30, 51.96) * mm, "radius": 7 * mm});
            skCircle(sketch, "E14.2.0", {"center": v(-30, 51.96) * mm, "radius": 5 * mm});
            skCircle(sketch, "E14.2.1", {"center": v(-30, 51.96) * mm, "radius": 7 * mm});
            skCircle(sketch, "E14.3.0", {"center": v(-60, 0) * mm, "radius": 5 * mm});
            skCircle(sketch, "E14.3.1", {"center": v(-60, 0) * mm, "radius": 7 * mm});
            skCircle(sketch, "E14.4.0", {"center": v(-30, -51.96) * mm, "radius": 5 * mm});
            skCircle(sketch, "E14.4.1", {"center": v(-30, -51.96) * mm, "radius": 7 * mm});
            skCircle(sketch, "E14.5.0", {"center": v(30, -51.96) * mm, "radius": 5 * mm});
            skCircle(sketch, "E14.5.1", {"center": v(30, -51.96) * mm, "radius": 7 * mm});
            skLineSegment(sketch, "E15.bottom", {"start": v(10, 3.5) * mm, "end": v(12, 3.5) * mm});
            skLineSegment(sketch, "E15.top", {"start": v(10, -3.5) * mm, "end": v(12, -3.5) * mm});
            skLineSegment(sketch, "E15.left", {"start": v(10, 3.5) * mm, "end": v(10, -3.5) * mm});
            skLineSegment(sketch, "E15.right", {"start": v(12, 3.5) * mm, "end": v(12, -3.5) * mm});
            skLineSegment(sketch, "E16.1.0.0", {"start": v(17.5, -3.5) * mm, "end": v(19.5, -3.5) * mm});
            skLineSegment(sketch, "E16.1.0.1", {"start": v(19.5, 3.5) * mm, "end": v(19.5, -3.5) * mm});
            skLineSegment(sketch, "E16.1.0.2", {"start": v(17.5, 3.5) * mm, "end": v(17.5, -3.5) * mm});
            skLineSegment(sketch, "E16.1.0.3", {"start": v(17.5, 3.5) * mm, "end": v(19.5, 3.5) * mm});
            skLineSegment(sketch, "E16.2.0.0", {"start": v(25, -3.5) * mm, "end": v(27, -3.5) * mm});
            skLineSegment(sketch, "E16.2.0.1", {"start": v(27, 3.5) * mm, "end": v(27, -3.5) * mm});
            skLineSegment(sketch, "E16.2.0.2", {"start": v(25, 3.5) * mm, "end": v(25, -3.5) * mm});
            skLineSegment(sketch, "E16.2.0.3", {"start": v(25, 3.5) * mm, "end": v(27, 3.5) * mm});
            skLineSegment(sketch, "E16.3.0.0", {"start": v(32.5, -3.5) * mm, "end": v(34.5, -3.5) * mm});
            skLineSegment(sketch, "E16.3.0.1", {"start": v(34.5, 3.5) * mm, "end": v(34.5, -3.5) * mm});
            skLineSegment(sketch, "E16.3.0.2", {"start": v(32.5, 3.5) * mm, "end": v(32.5, -3.5) * mm});
            skLineSegment(sketch, "E16.3.0.3", {"start": v(32.5, 3.5) * mm, "end": v(34.5, 3.5) * mm});
            skLineSegment(sketch, "E16.4.0.0", {"start": v(40, -3.5) * mm, "end": v(42, -3.5) * mm});
            skLineSegment(sketch, "E16.4.0.1", {"start": v(42, 3.5) * mm, "end": v(42, -3.5) * mm});
            skLineSegment(sketch, "E16.4.0.2", {"start": v(40, 3.5) * mm, "end": v(40, -3.5) * mm});
            skLineSegment(sketch, "E16.4.0.3", {"start": v(40, 3.5) * mm, "end": v(42, 3.5) * mm});
            skLineSegment(sketch, "E16.5.0.0", {"start": v(47.5, -3.5) * mm, "end": v(49.5, -3.5) * mm});
            skLineSegment(sketch, "E16.5.0.1", {"start": v(49.5, 3.5) * mm, "end": v(49.5, -3.5) * mm});
            skLineSegment(sketch, "E16.5.0.2", {"start": v(47.5, 3.5) * mm, "end": v(47.5, -3.5) * mm});
            skLineSegment(sketch, "E16.5.0.3", {"start": v(47.5, 3.5) * mm, "end": v(49.5, 3.5) * mm});
            skLineSegment(sketch, "E16.direction1", {"start": v(10, -3.5) * mm, "end": v(17.5, -3.5) * mm, "construction": true});
            skLineSegment(sketch, "E17.1.0", {"start": v(8.03, 6.91) * mm, "end": v(11.78, 13.4) * mm, "construction": true});
            skLineSegment(sketch, "E17.1.1", {"start": v(21.72, 44.61) * mm, "end": v(27.78, 41.12) * mm});
            skLineSegment(sketch, "E17.1.2", {"start": v(16.97, 36.39) * mm, "end": v(23.03, 32.9) * mm});
            skLineSegment(sketch, "E17.1.3", {"start": v(17.97, 38.12) * mm, "end": v(24.03, 34.62) * mm});
            skLineSegment(sketch, "E17.1.4", {"start": v(20.72, 42.88) * mm, "end": v(26.78, 39.39) * mm});
            skLineSegment(sketch, "E17.1.5", {"start": v(13.22, 29.9) * mm, "end": v(19.28, 26.4) * mm});
            skLineSegment(sketch, "E17.1.6", {"start": v(14.22, 31.62) * mm, "end": v(20.28, 28.13) * mm});
            skLineSegment(sketch, "E17.1.7", {"start": v(9.47, 23.4) * mm, "end": v(15.53, 19.9) * mm});
            skLineSegment(sketch, "E17.1.8", {"start": v(10.47, 25.13) * mm, "end": v(16.53, 21.63) * mm});
            skLineSegment(sketch, "E17.1.9", {"start": v(5.72, 16.9) * mm, "end": v(11.78, 13.4) * mm});
            skLineSegment(sketch, "E17.1.10", {"start": v(6.72, 18.63) * mm, "end": v(12.78, 15.14) * mm});
            skLineSegment(sketch, "E17.1.11", {"start": v(1.97, 10.4) * mm, "end": v(8.03, 6.91) * mm});
            skLineSegment(sketch, "E17.1.12", {"start": v(2.97, 12.14) * mm, "end": v(9.03, 8.64) * mm});
            skLineSegment(sketch, "E17.1.13", {"start": v(26.78, 39.39) * mm, "end": v(27.78, 41.12) * mm});
            skLineSegment(sketch, "E17.1.14", {"start": v(23.03, 32.9) * mm, "end": v(24.03, 34.62) * mm});
            skLineSegment(sketch, "E17.1.15", {"start": v(19.28, 26.4) * mm, "end": v(20.28, 28.13) * mm});
            skLineSegment(sketch, "E17.1.16", {"start": v(15.53, 19.9) * mm, "end": v(16.53, 21.63) * mm});
            skLineSegment(sketch, "E17.1.17", {"start": v(11.78, 13.4) * mm, "end": v(12.78, 15.14) * mm});
            skLineSegment(sketch, "E17.1.18", {"start": v(8.03, 6.91) * mm, "end": v(9.03, 8.64) * mm});
            skLineSegment(sketch, "E17.1.19", {"start": v(20.72, 42.88) * mm, "end": v(21.72, 44.61) * mm});
            skLineSegment(sketch, "E17.1.20", {"start": v(16.97, 36.39) * mm, "end": v(17.97, 38.12) * mm});
            skLineSegment(sketch, "E17.1.21", {"start": v(13.22, 29.9) * mm, "end": v(14.22, 31.62) * mm});
            skLineSegment(sketch, "E17.1.22", {"start": v(9.47, 23.4) * mm, "end": v(10.47, 25.13) * mm});
            skLineSegment(sketch, "E17.1.23", {"start": v(1.97, 10.4) * mm, "end": v(2.97, 12.14) * mm});
            skLineSegment(sketch, "E17.1.24", {"start": v(5.72, 16.9) * mm, "end": v(6.72, 18.63) * mm});
            skLineSegment(sketch, "E17.2.0", {"start": v(-1.97, 10.41) * mm, "end": v(-5.72, 16.9) * mm, "construction": true});
            skLineSegment(sketch, "E17.2.1", {"start": v(-27.78, 41.12) * mm, "end": v(-21.72, 44.62) * mm});
            skLineSegment(sketch, "E17.2.2", {"start": v(-23.03, 32.9) * mm, "end": v(-16.97, 36.4) * mm});
            skLineSegment(sketch, "E17.2.3", {"start": v(-24.03, 34.63) * mm, "end": v(-17.97, 38.12) * mm});
            skLineSegment(sketch, "E17.2.4", {"start": v(-26.78, 39.39) * mm, "end": v(-20.72, 42.89) * mm});
            skLineSegment(sketch, "E17.2.5", {"start": v(-19.28, 26.4) * mm, "end": v(-13.22, 29.9) * mm});
            skLineSegment(sketch, "E17.2.6", {"start": v(-20.28, 28.13) * mm, "end": v(-14.22, 31.63) * mm});
            skLineSegment(sketch, "E17.2.7", {"start": v(-15.53, 19.9) * mm, "end": v(-9.47, 23.4) * mm});
            skLineSegment(sketch, "E17.2.8", {"start": v(-16.53, 21.64) * mm, "end": v(-10.47, 25.13) * mm});
            skLineSegment(sketch, "E17.2.9", {"start": v(-11.78, 13.4) * mm, "end": v(-5.72, 16.9) * mm});
            skLineSegment(sketch, "E17.2.10", {"start": v(-12.78, 15.14) * mm, "end": v(-6.72, 18.64) * mm});
            skLineSegment(sketch, "E17.2.11", {"start": v(-8.03, 6.91) * mm, "end": v(-1.97, 10.41) * mm});
            skLineSegment(sketch, "E17.2.12", {"start": v(-9.03, 8.65) * mm, "end": v(-2.97, 12.14) * mm});
            skLineSegment(sketch, "E17.2.13", {"start": v(-20.72, 42.89) * mm, "end": v(-21.72, 44.62) * mm});
            skLineSegment(sketch, "E17.2.14", {"start": v(-16.97, 36.4) * mm, "end": v(-17.97, 38.12) * mm});
            skLineSegment(sketch, "E17.2.15", {"start": v(-13.22, 29.9) * mm, "end": v(-14.22, 31.63) * mm});
            skLineSegment(sketch, "E17.2.16", {"start": v(-9.47, 23.4) * mm, "end": v(-10.47, 25.13) * mm});
            skLineSegment(sketch, "E17.2.17", {"start": v(-5.72, 16.9) * mm, "end": v(-6.72, 18.64) * mm});
            skLineSegment(sketch, "E17.2.18", {"start": v(-1.97, 10.41) * mm, "end": v(-2.97, 12.14) * mm});
            skLineSegment(sketch, "E17.2.19", {"start": v(-26.78, 39.39) * mm, "end": v(-27.78, 41.12) * mm});
            skLineSegment(sketch, "E17.2.20", {"start": v(-23.03, 32.9) * mm, "end": v(-24.03, 34.63) * mm});
            skLineSegment(sketch, "E17.2.21", {"start": v(-19.28, 26.4) * mm, "end": v(-20.28, 28.13) * mm});
            skLineSegment(sketch, "E17.2.22", {"start": v(-15.53, 19.9) * mm, "end": v(-16.53, 21.64) * mm});
            skLineSegment(sketch, "E17.2.23", {"start": v(-8.03, 6.91) * mm, "end": v(-9.03, 8.65) * mm});
            skLineSegment(sketch, "E17.2.24", {"start": v(-11.78, 13.4) * mm, "end": v(-12.78, 15.14) * mm});
            skLineSegment(sketch, "E17.3.0", {"start": v(-10, 3.5) * mm, "end": v(-17.5, 3.5) * mm, "construction": true});
            skLineSegment(sketch, "E17.3.1", {"start": v(-49.5, -3.5) * mm, "end": v(-49.5, 3.5) * mm});
            skLineSegment(sketch, "E17.3.2", {"start": v(-40, -3.5) * mm, "end": v(-40, 3.5) * mm});
            skLineSegment(sketch, "E17.3.3", {"start": v(-42, -3.5) * mm, "end": v(-42, 3.5) * mm});
            skLineSegment(sketch, "E17.3.4", {"start": v(-47.5, -3.5) * mm, "end": v(-47.5, 3.5) * mm});
            skLineSegment(sketch, "E17.3.5", {"start": v(-32.5, -3.5) * mm, "end": v(-32.5, 3.5) * mm});
            skLineSegment(sketch, "E17.3.6", {"start": v(-34.5, -3.5) * mm, "end": v(-34.5, 3.5) * mm});
            skLineSegment(sketch, "E17.3.7", {"start": v(-25, -3.5) * mm, "end": v(-25, 3.5) * mm});
            skLineSegment(sketch, "E17.3.8", {"start": v(-27, -3.5) * mm, "end": v(-27, 3.5) * mm});
            skLineSegment(sketch, "E17.3.9", {"start": v(-17.5, -3.5) * mm, "end": v(-17.5, 3.5) * mm});
            skLineSegment(sketch, "E17.3.10", {"start": v(-19.5, -3.5) * mm, "end": v(-19.5, 3.5) * mm});
            skLineSegment(sketch, "E17.3.11", {"start": v(-10, -3.5) * mm, "end": v(-10, 3.5) * mm});
            skLineSegment(sketch, "E17.3.12", {"start": v(-12, -3.5) * mm, "end": v(-12, 3.5) * mm});
            skLineSegment(sketch, "E17.3.13", {"start": v(-47.5, 3.5) * mm, "end": v(-49.5, 3.5) * mm});
            skLineSegment(sketch, "E17.3.14", {"start": v(-40, 3.5) * mm, "end": v(-42, 3.5) * mm});
            skLineSegment(sketch, "E17.3.15", {"start": v(-32.5, 3.5) * mm, "end": v(-34.5, 3.5) * mm});
            skLineSegment(sketch, "E17.3.16", {"start": v(-25, 3.5) * mm, "end": v(-27, 3.5) * mm});
            skLineSegment(sketch, "E17.3.17", {"start": v(-17.5, 3.5) * mm, "end": v(-19.5, 3.5) * mm});
            skLineSegment(sketch, "E17.3.18", {"start": v(-10, 3.5) * mm, "end": v(-12, 3.5) * mm});
            skLineSegment(sketch, "E17.3.19", {"start": v(-47.5, -3.5) * mm, "end": v(-49.5, -3.5) * mm});
            skLineSegment(sketch, "E17.3.20", {"start": v(-40, -3.5) * mm, "end": v(-42, -3.5) * mm});
            skLineSegment(sketch, "E17.3.21", {"start": v(-32.5, -3.5) * mm, "end": v(-34.5, -3.5) * mm});
            skLineSegment(sketch, "E17.3.22", {"start": v(-25, -3.5) * mm, "end": v(-27, -3.5) * mm});
            skLineSegment(sketch, "E17.3.23", {"start": v(-10, -3.5) * mm, "end": v(-12, -3.5) * mm});
            skLineSegment(sketch, "E17.3.24", {"start": v(-17.5, -3.5) * mm, "end": v(-19.5, -3.5) * mm});
            skLineSegment(sketch, "E17.4.0", {"start": v(-8.03, -6.91) * mm, "end": v(-11.78, -13.4) * mm, "construction": true});
            skLineSegment(sketch, "E17.4.1", {"start": v(-21.72, -44.61) * mm, "end": v(-27.78, -41.12) * mm});
            skLineSegment(sketch, "E17.4.2", {"start": v(-16.97, -36.39) * mm, "end": v(-23.03, -32.9) * mm});
            skLineSegment(sketch, "E17.4.3", {"start": v(-17.97, -38.12) * mm, "end": v(-24.03, -34.62) * mm});
            skLineSegment(sketch, "E17.4.4", {"start": v(-20.72, -42.88) * mm, "end": v(-26.78, -39.39) * mm});
            skLineSegment(sketch, "E17.4.5", {"start": v(-13.22, -29.9) * mm, "end": v(-19.28, -26.4) * mm});
            skLineSegment(sketch, "E17.4.6", {"start": v(-14.22, -31.62) * mm, "end": v(-20.28, -28.13) * mm});
            skLineSegment(sketch, "E17.4.7", {"start": v(-9.47, -23.4) * mm, "end": v(-15.53, -19.9) * mm});
            skLineSegment(sketch, "E17.4.8", {"start": v(-10.47, -25.13) * mm, "end": v(-16.53, -21.63) * mm});
            skLineSegment(sketch, "E17.4.9", {"start": v(-5.72, -16.9) * mm, "end": v(-11.78, -13.4) * mm});
            skLineSegment(sketch, "E17.4.10", {"start": v(-6.72, -18.63) * mm, "end": v(-12.78, -15.14) * mm});
            skLineSegment(sketch, "E17.4.11", {"start": v(-1.97, -10.4) * mm, "end": v(-8.03, -6.91) * mm});
            skLineSegment(sketch, "E17.4.12", {"start": v(-2.97, -12.14) * mm, "end": v(-9.03, -8.64) * mm});
            skLineSegment(sketch, "E17.4.13", {"start": v(-26.78, -39.39) * mm, "end": v(-27.78, -41.12) * mm});
            skLineSegment(sketch, "E17.4.14", {"start": v(-23.03, -32.9) * mm, "end": v(-24.03, -34.62) * mm});
            skLineSegment(sketch, "E17.4.15", {"start": v(-19.28, -26.4) * mm, "end": v(-20.28, -28.13) * mm});
            skLineSegment(sketch, "E17.4.16", {"start": v(-15.53, -19.9) * mm, "end": v(-16.53, -21.63) * mm});
            skLineSegment(sketch, "E17.4.17", {"start": v(-11.78, -13.4) * mm, "end": v(-12.78, -15.14) * mm});
            skLineSegment(sketch, "E17.4.18", {"start": v(-8.03, -6.91) * mm, "end": v(-9.03, -8.64) * mm});
            skLineSegment(sketch, "E17.4.19", {"start": v(-20.72, -42.88) * mm, "end": v(-21.72, -44.61) * mm});
            skLineSegment(sketch, "E17.4.20", {"start": v(-16.97, -36.39) * mm, "end": v(-17.97, -38.12) * mm});
            skLineSegment(sketch, "E17.4.21", {"start": v(-13.22, -29.9) * mm, "end": v(-14.22, -31.62) * mm});
            skLineSegment(sketch, "E17.4.22", {"start": v(-9.47, -23.4) * mm, "end": v(-10.47, -25.13) * mm});
            skLineSegment(sketch, "E17.4.23", {"start": v(-1.97, -10.4) * mm, "end": v(-2.97, -12.14) * mm});
            skLineSegment(sketch, "E17.4.24", {"start": v(-5.72, -16.9) * mm, "end": v(-6.72, -18.63) * mm});
            skLineSegment(sketch, "E17.5.0", {"start": v(1.97, -10.41) * mm, "end": v(5.72, -16.9) * mm, "construction": true});
            skLineSegment(sketch, "E17.5.1", {"start": v(27.78, -41.12) * mm, "end": v(21.72, -44.62) * mm});
            skLineSegment(sketch, "E17.5.2", {"start": v(23.03, -32.9) * mm, "end": v(16.97, -36.4) * mm});
            skLineSegment(sketch, "E17.5.3", {"start": v(24.03, -34.63) * mm, "end": v(17.97, -38.12) * mm});
            skLineSegment(sketch, "E17.5.4", {"start": v(26.78, -39.39) * mm, "end": v(20.72, -42.89) * mm});
            skLineSegment(sketch, "E17.5.5", {"start": v(19.28, -26.4) * mm, "end": v(13.22, -29.9) * mm});
            skLineSegment(sketch, "E17.5.6", {"start": v(20.28, -28.13) * mm, "end": v(14.22, -31.63) * mm});
            skLineSegment(sketch, "E17.5.7", {"start": v(15.53, -19.9) * mm, "end": v(9.47, -23.4) * mm});
            skLineSegment(sketch, "E17.5.8", {"start": v(16.53, -21.64) * mm, "end": v(10.47, -25.13) * mm});
            skLineSegment(sketch, "E17.5.9", {"start": v(11.78, -13.4) * mm, "end": v(5.72, -16.9) * mm});
            skLineSegment(sketch, "E17.5.10", {"start": v(12.78, -15.14) * mm, "end": v(6.72, -18.64) * mm});
            skLineSegment(sketch, "E17.5.11", {"start": v(8.03, -6.91) * mm, "end": v(1.97, -10.41) * mm});
            skLineSegment(sketch, "E17.5.12", {"start": v(9.03, -8.65) * mm, "end": v(2.97, -12.14) * mm});
            skLineSegment(sketch, "E17.5.13", {"start": v(20.72, -42.89) * mm, "end": v(21.72, -44.62) * mm});
            skLineSegment(sketch, "E17.5.14", {"start": v(16.97, -36.4) * mm, "end": v(17.97, -38.12) * mm});
            skLineSegment(sketch, "E17.5.15", {"start": v(13.22, -29.9) * mm, "end": v(14.22, -31.63) * mm});
            skLineSegment(sketch, "E17.5.16", {"start": v(9.47, -23.4) * mm, "end": v(10.47, -25.13) * mm});
            skLineSegment(sketch, "E17.5.17", {"start": v(5.72, -16.9) * mm, "end": v(6.72, -18.64) * mm});
            skLineSegment(sketch, "E17.5.18", {"start": v(1.97, -10.41) * mm, "end": v(2.97, -12.14) * mm});
            skLineSegment(sketch, "E17.5.19", {"start": v(26.78, -39.39) * mm, "end": v(27.78, -41.12) * mm});
            skLineSegment(sketch, "E17.5.20", {"start": v(23.03, -32.9) * mm, "end": v(24.03, -34.63) * mm});
            skLineSegment(sketch, "E17.5.21", {"start": v(19.28, -26.4) * mm, "end": v(20.28, -28.13) * mm});
            skLineSegment(sketch, "E17.5.22", {"start": v(15.53, -19.9) * mm, "end": v(16.53, -21.64) * mm});
            skLineSegment(sketch, "E17.5.23", {"start": v(8.03, -6.91) * mm, "end": v(9.03, -8.65) * mm});
            skLineSegment(sketch, "E17.5.24", {"start": v(11.78, -13.4) * mm, "end": v(12.78, -15.14) * mm});
            skPoint(sketch, "E17.center", {"position": v(0, 0) * mm});
            skSolve(sketch);
        }
        {
            var Q0;
            Q0=makeQuery(id+"F4.imprint","IMPRINT",FACE,{"disambiguationData":[TD([[makeQuery(id+"F4.imprint","IMPRINT",EDGE,{"derivedFrom":sQuery(id+"F4.wireOp",EDGE,"E17.5.11")}),1.0]])]});
            var Q1;
            Q1=makeQuery(id+"F4.imprint","IMPRINT",FACE,{"disambiguationData":[TD([[makeQuery(id+"F4.imprint","IMPRINT",EDGE,{"derivedFrom":sQuery(id+"F4.wireOp",EDGE,"E17.5.9")}),1.0]])]});
            var Q2;
            Q2=makeQuery(id+"F4.imprint","IMPRINT",FACE,{"disambiguationData":[TD([[makeQuery(id+"F4.imprint","IMPRINT",EDGE,{"derivedFrom":sQuery(id+"F4.wireOp",EDGE,"E17.5.7")}),1.0]])]});
            var Q3;
            Q3=makeQuery(id+"F4.imprint","IMPRINT",FACE,{"disambiguationData":[TD([[makeQuery(id+"F4.imprint","IMPRINT",EDGE,{"derivedFrom":sQuery(id+"F4.wireOp",EDGE,"E17.5.5")}),1.0]])]});
            var Q4;
            Q4=makeQuery(id+"F4.imprint","IMPRINT",FACE,{"disambiguationData":[TD([[makeQuery(id+"F4.imprint","IMPRINT",EDGE,{"derivedFrom":sQuery(id+"F4.wireOp",EDGE,"E17.5.2")}),1.0]])]});
            var Q5;
            Q5=makeQuery(id+"F4.imprint","IMPRINT",FACE,{"disambiguationData":[TD([[makeQuery(id+"F4.imprint","IMPRINT",EDGE,{"derivedFrom":sQuery(id+"F4.wireOp",EDGE,"E17.5.1")}),-1.0]])]});
            var Q6;
            Q6=makeQuery(id+"F4.imprint","IMPRINT",FACE,{"disambiguationData":[TD([[makeQuery(id+"F4.imprint","IMPRINT",EDGE,{"derivedFrom":sQuery(id+"F4.wireOp",EDGE,"E15.bottom")}),-1.0]])]});
            var Q7;
            Q7=makeQuery(id+"F4.imprint","IMPRINT",FACE,{"disambiguationData":[TD([[makeQuery(id+"F4.imprint","IMPRINT",EDGE,{"derivedFrom":sQuery(id+"F4.wireOp",EDGE,"E16.1.0.0")}),1.0]])]});
            var Q8;
            Q8=makeQuery(id+"F4.imprint","IMPRINT",FACE,{"disambiguationData":[TD([[makeQuery(id+"F4.imprint","IMPRINT",EDGE,{"derivedFrom":sQuery(id+"F4.wireOp",EDGE,"E16.2.0.0")}),1.0]])]});
            var Q9;
            Q9=makeQuery(id+"F4.imprint","IMPRINT",FACE,{"disambiguationData":[TD([[makeQuery(id+"F4.imprint","IMPRINT",EDGE,{"derivedFrom":sQuery(id+"F4.wireOp",EDGE,"E16.3.0.0")}),1.0]])]});
            var Q10;
            Q10=makeQuery(id+"F4.imprint","IMPRINT",FACE,{"disambiguationData":[TD([[makeQuery(id+"F4.imprint","IMPRINT",EDGE,{"derivedFrom":sQuery(id+"F4.wireOp",EDGE,"E16.4.0.0")}),1.0]])]});
            var Q11;
            Q11=makeQuery(id+"F4.imprint","IMPRINT",FACE,{"disambiguationData":[TD([[makeQuery(id+"F4.imprint","IMPRINT",EDGE,{"derivedFrom":sQuery(id+"F4.wireOp",EDGE,"E16.5.0.0")}),1.0]])]});
            var Q12;
            Q12=makeQuery(id+"F4.imprint","IMPRINT",FACE,{"disambiguationData":[TD([[makeQuery(id+"F4.imprint","IMPRINT",EDGE,{"derivedFrom":sQuery(id+"F4.wireOp",EDGE,"E17.1.1")}),-1.0]])]});
            var Q13;
            Q13=makeQuery(id+"F4.imprint","IMPRINT",FACE,{"disambiguationData":[TD([[makeQuery(id+"F4.imprint","IMPRINT",EDGE,{"derivedFrom":sQuery(id+"F4.wireOp",EDGE,"E17.1.2")}),1.0]])]});
            var Q14;
            Q14=makeQuery(id+"F4.imprint","IMPRINT",FACE,{"disambiguationData":[TD([[makeQuery(id+"F4.imprint","IMPRINT",EDGE,{"derivedFrom":sQuery(id+"F4.wireOp",EDGE,"E17.1.5")}),1.0]])]});
            var Q15;
            Q15=makeQuery(id+"F4.imprint","IMPRINT",FACE,{"disambiguationData":[TD([[makeQuery(id+"F4.imprint","IMPRINT",EDGE,{"derivedFrom":sQuery(id+"F4.wireOp",EDGE,"E17.1.7")}),1.0]])]});
            var Q16;
            Q16=makeQuery(id+"F4.imprint","IMPRINT",FACE,{"disambiguationData":[TD([[makeQuery(id+"F4.imprint","IMPRINT",EDGE,{"derivedFrom":sQuery(id+"F4.wireOp",EDGE,"E17.1.9")}),1.0]])]});
            var Q17;
            Q17=makeQuery(id+"F4.imprint","IMPRINT",FACE,{"disambiguationData":[TD([[makeQuery(id+"F4.imprint","IMPRINT",EDGE,{"derivedFrom":sQuery(id+"F4.wireOp",EDGE,"E17.1.11")}),1.0]])]});
            var Q18;
            Q18=makeQuery(id+"F4.imprint","IMPRINT",FACE,{"disambiguationData":[TD([[makeQuery(id+"F4.imprint","IMPRINT",EDGE,{"derivedFrom":sQuery(id+"F4.wireOp",EDGE,"E17.4.11")}),1.0]])]});
            var Q19;
            Q19=makeQuery(id+"F4.imprint","IMPRINT",FACE,{"disambiguationData":[TD([[makeQuery(id+"F4.imprint","IMPRINT",EDGE,{"derivedFrom":sQuery(id+"F4.wireOp",EDGE,"E17.4.9")}),1.0]])]});
            var Q20;
            Q20=makeQuery(id+"F4.imprint","IMPRINT",FACE,{"disambiguationData":[TD([[makeQuery(id+"F4.imprint","IMPRINT",EDGE,{"derivedFrom":sQuery(id+"F4.wireOp",EDGE,"E17.4.7")}),1.0]])]});
            var Q21;
            Q21=makeQuery(id+"F4.imprint","IMPRINT",FACE,{"disambiguationData":[TD([[makeQuery(id+"F4.imprint","IMPRINT",EDGE,{"derivedFrom":sQuery(id+"F4.wireOp",EDGE,"E17.4.5")}),1.0]])]});
            var Q22;
            Q22=makeQuery(id+"F4.imprint","IMPRINT",FACE,{"disambiguationData":[TD([[makeQuery(id+"F4.imprint","IMPRINT",EDGE,{"derivedFrom":sQuery(id+"F4.wireOp",EDGE,"E17.4.2")}),1.0]])]});
            var Q23;
            Q23=makeQuery(id+"F4.imprint","IMPRINT",FACE,{"disambiguationData":[TD([[makeQuery(id+"F4.imprint","IMPRINT",EDGE,{"derivedFrom":sQuery(id+"F4.wireOp",EDGE,"E17.4.1")}),-1.0]])]});
            var Q24;
            Q24=makeQuery(id+"F4.imprint","IMPRINT",FACE,{"disambiguationData":[TD([[makeQuery(id+"F4.imprint","IMPRINT",EDGE,{"derivedFrom":sQuery(id+"F4.wireOp",EDGE,"E17.3.1")}),-1.0]])]});
            var Q25;
            Q25=makeQuery(id+"F4.imprint","IMPRINT",FACE,{"disambiguationData":[TD([[makeQuery(id+"F4.imprint","IMPRINT",EDGE,{"derivedFrom":sQuery(id+"F4.wireOp",EDGE,"E17.3.2")}),1.0]])]});
            var Q26;
            Q26=makeQuery(id+"F4.imprint","IMPRINT",FACE,{"disambiguationData":[TD([[makeQuery(id+"F4.imprint","IMPRINT",EDGE,{"derivedFrom":sQuery(id+"F4.wireOp",EDGE,"E17.3.5")}),1.0]])]});
            var Q27;
            Q27=makeQuery(id+"F4.imprint","IMPRINT",FACE,{"disambiguationData":[TD([[makeQuery(id+"F4.imprint","IMPRINT",EDGE,{"derivedFrom":sQuery(id+"F4.wireOp",EDGE,"E17.3.7")}),1.0]])]});
            var Q28;
            Q28=makeQuery(id+"F4.imprint","IMPRINT",FACE,{"disambiguationData":[TD([[makeQuery(id+"F4.imprint","IMPRINT",EDGE,{"derivedFrom":sQuery(id+"F4.wireOp",EDGE,"E17.3.9")}),1.0]])]});
            var Q29;
            Q29=makeQuery(id+"F4.imprint","IMPRINT",FACE,{"disambiguationData":[TD([[makeQuery(id+"F4.imprint","IMPRINT",EDGE,{"derivedFrom":sQuery(id+"F4.wireOp",EDGE,"E17.3.11")}),1.0]])]});
            var Q30;
            Q30=makeQuery(id+"F4.imprint","IMPRINT",FACE,{"disambiguationData":[TD([[makeQuery(id+"F4.imprint","IMPRINT",EDGE,{"derivedFrom":sQuery(id+"F4.wireOp",EDGE,"E17.2.2")}),1.0]])]});
            var Q31;
            Q31=makeQuery(id+"F4.imprint","IMPRINT",FACE,{"disambiguationData":[TD([[makeQuery(id+"F4.imprint","IMPRINT",EDGE,{"derivedFrom":sQuery(id+"F4.wireOp",EDGE,"E17.2.5")}),1.0]])]});
            var Q32;
            Q32=makeQuery(id+"F4.imprint","IMPRINT",FACE,{"disambiguationData":[TD([[makeQuery(id+"F4.imprint","IMPRINT",EDGE,{"derivedFrom":sQuery(id+"F4.wireOp",EDGE,"E17.2.11")}),1.0]])]});
            var Q33;
            Q33=makeQuery(id+"F4.imprint","IMPRINT",FACE,{"disambiguationData":[TD([[makeQuery(id+"F4.imprint","IMPRINT",EDGE,{"derivedFrom":sQuery(id+"F4.wireOp",EDGE,"E17.2.1")}),-1.0]])]});
            var Q34;
            Q34=makeQuery(id+"F4.imprint","IMPRINT",FACE,{"disambiguationData":[TD([[makeQuery(id+"F4.imprint","IMPRINT",EDGE,{"derivedFrom":sQuery(id+"F4.wireOp",EDGE,"E17.2.7")}),1.0]])]});
            var Q35;
            Q35=makeQuery(id+"F4.imprint","IMPRINT",FACE,{"disambiguationData":[TD([[makeQuery(id+"F4.imprint","IMPRINT",EDGE,{"derivedFrom":sQuery(id+"F4.wireOp",EDGE,"E17.2.9")}),1.0]])]});
            var Q36;
            Q36=makeQuery(id+"F4.imprint","IMPRINT",FACE,{"disambiguationData":[TD([[makeQuery(id+"F4.imprint","IMPRINT",EDGE,{"derivedFrom":sQuery(id+"F4.wireOp",EDGE,"E12")}),-1.0]])]});
            var Q37;
            Q37=makeQuery(id+"F4.imprint","IMPRINT",FACE,{"disambiguationData":[TD([[makeQuery(id+"F4.imprint","IMPRINT",EDGE,{"derivedFrom":sQuery(id+"F4.wireOp",EDGE,"E14.1.0")}),-1.0]])]});
            var Q38;
            Q38=makeQuery(id+"F4.imprint","IMPRINT",FACE,{"disambiguationData":[TD([[makeQuery(id+"F4.imprint","IMPRINT",EDGE,{"derivedFrom":sQuery(id+"F4.wireOp",EDGE,"E14.2.0")}),-1.0]])]});
            var Q39;
            Q39=makeQuery(id+"F4.imprint","IMPRINT",FACE,{"disambiguationData":[TD([[makeQuery(id+"F4.imprint","IMPRINT",EDGE,{"derivedFrom":sQuery(id+"F4.wireOp",EDGE,"E14.3.0")}),-1.0]])]});
            var Q40;
            Q40=makeQuery(id+"F4.imprint","IMPRINT",FACE,{"disambiguationData":[TD([[makeQuery(id+"F4.imprint","IMPRINT",EDGE,{"derivedFrom":sQuery(id+"F4.wireOp",EDGE,"E14.4.0")}),-1.0]])]});
            var Q41;
            Q41=makeQuery(id+"F4.imprint","IMPRINT",FACE,{"disambiguationData":[TD([[makeQuery(id+"F4.imprint","IMPRINT",EDGE,{"derivedFrom":sQuery(id+"F4.wireOp",EDGE,"E14.5.0")}),-1.0]])]});
            extrude(context, id + "F5", {"entities" : qUnion([Q0, Q1, Q2, Q3, Q4, Q5, Q6, Q7, Q8, Q9, Q10, Q11, Q12, Q13, Q14, Q15, Q16, Q17, Q18, Q19, Q20, Q21, Q22, Q23, Q24, Q25, Q26, Q27, Q28, Q29, Q30, Q31, Q32, Q33, Q34, Q35, Q36, Q37, Q38, Q39, Q40, Q41]), "operationType" : NewBodyOperationType.REMOVE, "oppositeDirection" : true, "depth" : 1 * mm, "offsetDistance" : 25 * mm});
        }
    });
